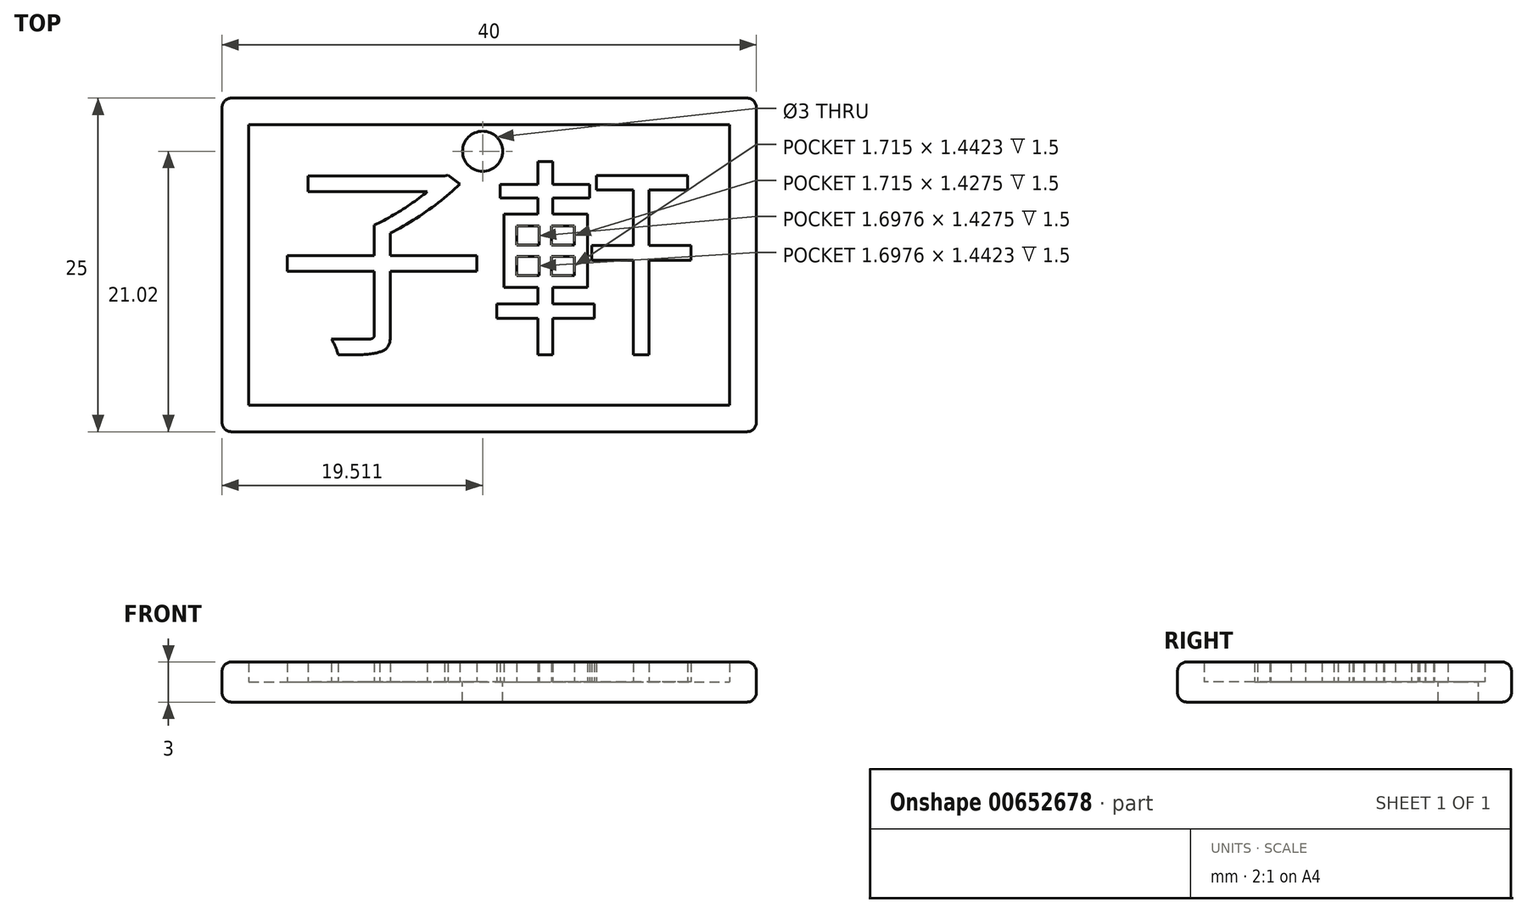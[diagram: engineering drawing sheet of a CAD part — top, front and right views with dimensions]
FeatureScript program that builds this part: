
annotation { "Feature Type Name" : "Feature", "Feature Type Description" : "" }
export const myFeature = defineFeature(function(context is Context, id is Id, definition is map)
    precondition{}
    {
        {
            var Q0;
            Q0=qCreatedBy(makeId("Top.planeOp"),FACE);
            var sketch = newSketch(context, id + "F0", { "sketchPlane" : qUnion([Q0])});
            skLineSegment(sketch, "E0.bottom", {"start": v(18.58, -13.36) * mm, "end": v(-21.42, -13.36) * mm});
            skLineSegment(sketch, "E0.top", {"start": v(18.58, 11.64) * mm, "end": v(-21.42, 11.64) * mm});
            skLineSegment(sketch, "E0.left", {"start": v(18.58, -13.36) * mm, "end": v(18.58, 11.64) * mm});
            skLineSegment(sketch, "E0.right", {"start": v(-21.42, -13.36) * mm, "end": v(-21.42, 11.64) * mm});
            skPoint(sketch, "E0.middle", {"position": v(0, 0) * mm});
            skSolve(sketch);
        }
        {
            var Q0;
            Q0 = qSketchRegion(id + "F0", true);
            extrude(context, id + "F1", {"entities" : qUnion([Q0]), "depth" : 1.5 * mm, "offsetDistance" : 25 * mm});
        }
        {
            var Q0;
            Q0=makeQuery(id+"F1.opExtrude","CAP_FACE",FACE,{"disambiguationData":[OSD([sQuery(id+"F0.wireOp",EDGE,"E0.bottom"),sQuery(id+"F0.wireOp",EDGE,"E0.top"),sQuery(id+"F0.wireOp",EDGE,"E0.left"),sQuery(id+"F0.wireOp",EDGE,"E0.right")])],"isStart":false});
            var sketch = newSketch(context, id + "F2", { "sketchPlane" : qUnion([Q0])});
            skLineSegment(sketch, "E1.bottom", {"start": v(-21.42, 11.64) * mm, "end": v(18.58, 11.64) * mm});
            skLineSegment(sketch, "E1.top", {"start": v(-21.42, -13.36) * mm, "end": v(18.58, -13.36) * mm});
            skLineSegment(sketch, "E1.left", {"start": v(-21.42, 11.64) * mm, "end": v(-21.42, -13.36) * mm});
            skLineSegment(sketch, "E1.right", {"start": v(18.58, 11.64) * mm, "end": v(18.58, -13.36) * mm});
            skLineSegment(sketch, "E2.0", {"start": v(-19.42, 9.64) * mm, "end": v(16.58, 9.64) * mm});
            skLineSegment(sketch, "E2.1", {"start": v(-19.42, 9.64) * mm, "end": v(-19.42, -11.36) * mm});
            skLineSegment(sketch, "E2.2", {"start": v(-19.42, -11.36) * mm, "end": v(16.58, -11.36) * mm});
            skLineSegment(sketch, "E2.3", {"start": v(16.58, 9.64) * mm, "end": v(16.58, -11.36) * mm});
            skSolve(sketch);
        }
        {
            var Q0;
            Q0 = qSketchRegion(id + "F2", true);
            extrude(context, id + "F3", {"entities" : qUnion([Q0]), "operationType" : NewBodyOperationType.ADD, "depth" : 1.5 * mm, "offsetDistance" : 25 * mm});
        }
        {
            var Q0;
            Q0=makeQuery(id+"F1.opExtrude","CAP_FACE",FACE,{"disambiguationData":[OSD([sQuery(id+"F0.wireOp",EDGE,"E0.bottom"),sQuery(id+"F0.wireOp",EDGE,"E0.top"),sQuery(id+"F0.wireOp",EDGE,"E0.left"),sQuery(id+"F0.wireOp",EDGE,"E0.right")])],"isStart":false});
            var sketch = newSketch(context, id + "F4", { "sketchPlane" : qUnion([Q0])});
            skText(sketch, "E3", { "text": "子軒", "fontName": "NotoSansCJKtc-Regular.otf"});
            const initialGuessF4  = {"E3": [-0.0174, -0.0064, 1, 0, 0.01142]};
            skSetInitialGuess(sketch, initialGuessF4);
            skSolve(sketch);
        }
        {
            var Q0;
            Q0 = qSketchRegion(id + "F4", true);
            extrude(context, id + "F5", {"entities" : qUnion([Q0]), "operationType" : NewBodyOperationType.ADD, "depth" : 1.5 * mm, "offsetDistance" : 25 * mm});
        }
        {
            var Q0;
            Q0=makeQuery(id+"F5.boolean.opBoolean","SPLIT",FACE,{"disambiguationData":[TD([makeQuery(id+"F3.opExtrude","SWEPT_FACE",FACE,{"disambiguationData":[OSD([sQuery(id+"F2.wireOp",EDGE,"E2.0")])]})])],"derivedFrom":makeQuery(id+"F1.opExtrude","CAP_FACE",FACE,{"disambiguationData":[OSD([sQuery(id+"F0.wireOp",EDGE,"E0.bottom"),sQuery(id+"F0.wireOp",EDGE,"E0.top"),sQuery(id+"F0.wireOp",EDGE,"E0.left"),sQuery(id+"F0.wireOp",EDGE,"E0.right")])],"isStart":false})});
            var sketch = newSketch(context, id + "F6", { "sketchPlane" : qUnion([Q0])});
            skCircle(sketch, "E4", {"center": v(-1.9, 7.66) * mm, "radius": 1.5 * mm});
            skSolve(sketch);
        }
        {
            var Q0;
            Q0 = qSketchRegion(id + "F6", true);
            extrude(context, id + "F7", {"entities" : qUnion([Q0]), "operationType" : NewBodyOperationType.REMOVE, "oppositeDirection" : true, "depth" : 25 * mm, "offsetDistance" : 25 * mm});
        }
        {
            var Q0;
            Q0=makeQuery(id+"F3.boolean.opBoolean","MERGE",FACE,{"derivedFrom":[makeQuery(id+"F1.opExtrude","SWEPT_FACE",FACE,{"disambiguationData":[OSD([sQuery(id+"F0.wireOp",EDGE,"E0.bottom")])]}),makeQuery(id+"F3.opExtrude","SWEPT_FACE",FACE,{"disambiguationData":[OSD([sQuery(id+"F2.wireOp",EDGE,"E1.top")])]})]});
            var Q1;
            Q1=makeQuery(id+"F3.boolean.opBoolean","MERGE",FACE,{"derivedFrom":[makeQuery(id+"F1.opExtrude","SWEPT_FACE",FACE,{"disambiguationData":[OSD([sQuery(id+"F0.wireOp",EDGE,"E0.right")])]}),makeQuery(id+"F3.opExtrude","SWEPT_FACE",FACE,{"disambiguationData":[OSD([sQuery(id+"F2.wireOp",EDGE,"E1.left")])]})]});
            var Q2;
            Q2=makeQuery(id+"F3.opExtrude","CAP_EDGE",EDGE,{"disambiguationData":[OSD([sQuery(id+"F2.wireOp",EDGE,"E1.bottom")])],"isStart":false});
            var Q3;
            Q3=makeQuery(id+"F3.opExtrude","CAP_EDGE",EDGE,{"disambiguationData":[OSD([sQuery(id+"F2.wireOp",EDGE,"E1.right")])],"isStart":false});
            var Q4;
            Q4=makeQuery(id+"F3.boolean.opBoolean","MERGE",EDGE,{"derivedFrom":[makeQuery(id+"F1.opExtrude","SWEPT_EDGE",EDGE,{"disambiguationData":[OSD([sQuery(id+"F0.wireOp",EDGE,"E0.top"),sQuery(id+"F0.wireOp",EDGE,"E0.left")])]}),makeQuery(id+"F3.opExtrude","SWEPT_EDGE",EDGE,{"disambiguationData":[OSD([sQuery(id+"F2.wireOp",EDGE,"E1.bottom"),sQuery(id+"F2.wireOp",EDGE,"E1.right")])]})]});
            var Q5;
            Q5=makeQuery(id+"F1.opExtrude","CAP_EDGE",EDGE,{"disambiguationData":[OSD([sQuery(id+"F0.wireOp",EDGE,"E0.left")])],"isStart":true});
            var Q6;
            Q6=makeQuery(id+"F1.opExtrude","CAP_EDGE",EDGE,{"disambiguationData":[OSD([sQuery(id+"F0.wireOp",EDGE,"E0.top")])],"isStart":true});
            fillet(context, id + "F8", {"entities" : qUnion([Q0, Q1, Q2, Q3, Q4, Q5, Q6]), "radius" : 0.7 * mm, "tangentPropagation" : true, "allowEdgeOverflow" : false});
        }
    });
